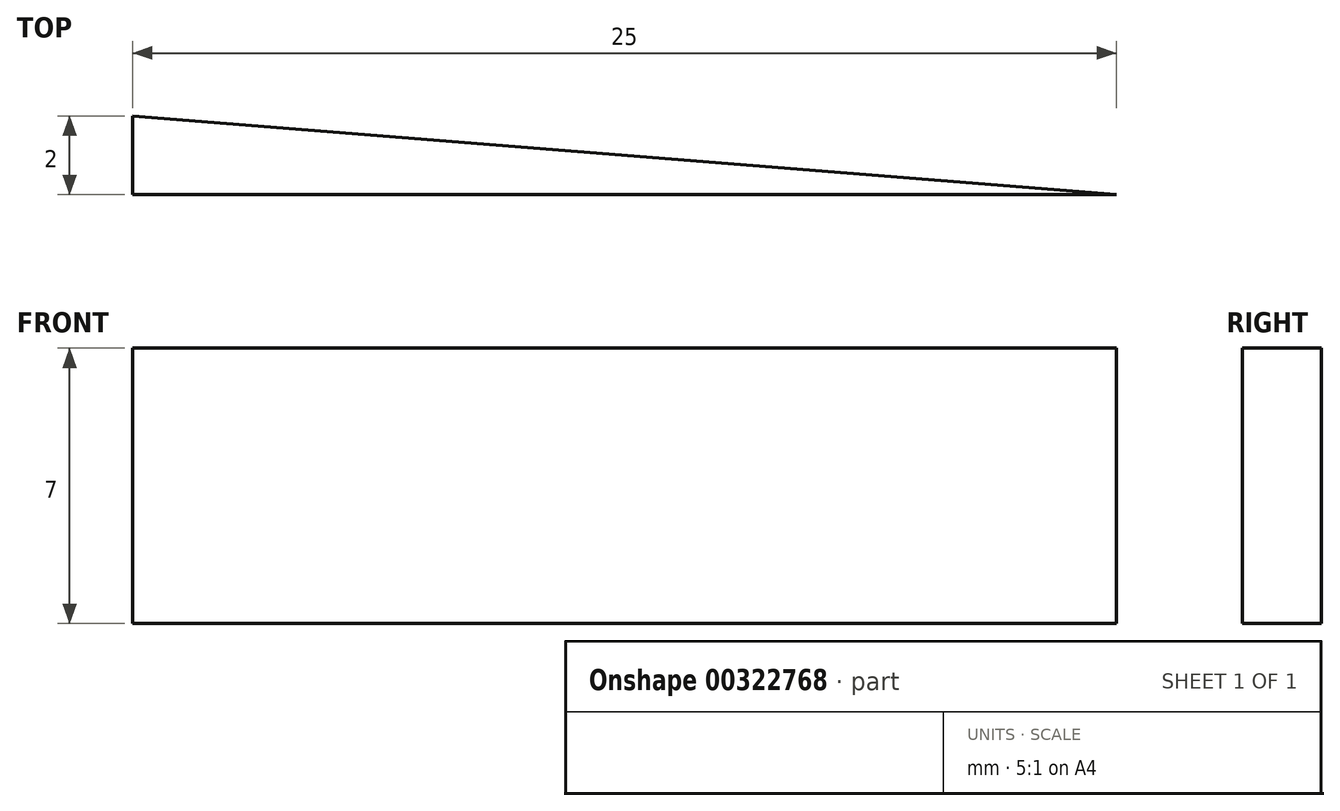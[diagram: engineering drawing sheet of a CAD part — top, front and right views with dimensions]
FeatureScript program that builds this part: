
annotation { "Feature Type Name" : "Feature", "Feature Type Description" : "" }
export const myFeature = defineFeature(function(context is Context, id is Id, definition is map)
    precondition{}
    {
        {
            var Q0;
            Q0=qCreatedBy(makeId("Top.planeOp"),FACE);
            var sketch = newSketch(context, id + "F0", { "sketchPlane" : qUnion([Q0])});
            skLineSegment(sketch, "E0", {"start": v(0, 0) * mm, "end": v(-25, 0) * mm});
            skLineSegment(sketch, "E1", {"start": v(-25, 0) * mm, "end": v(-25, 2) * mm});
            skLineSegment(sketch, "E2", {"start": v(-25, 2) * mm, "end": v(0, 0) * mm});
            skSolve(sketch);
        }
        {
            var Q0;
            Q0 = qSketchRegion(id + "F0", true);
            extrude(context, id + "F1", {"entities" : qUnion([Q0]), "depth" : 7 * mm});
        }
    });
